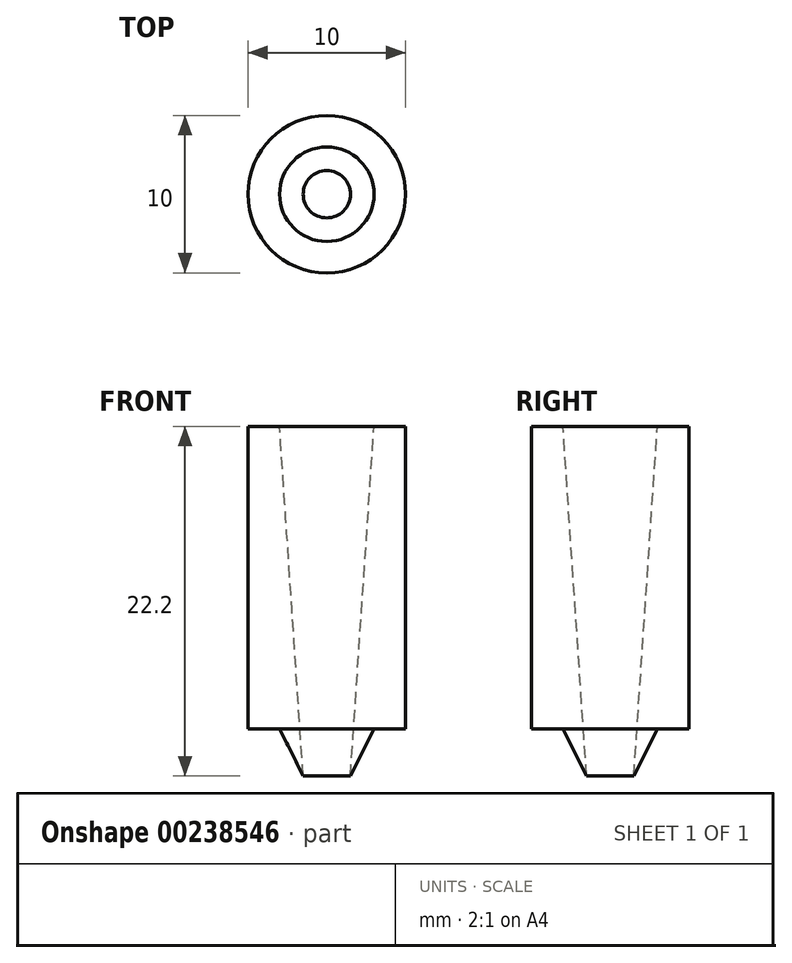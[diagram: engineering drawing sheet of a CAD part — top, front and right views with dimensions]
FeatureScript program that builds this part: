
annotation { "Feature Type Name" : "Feature", "Feature Type Description" : "" }
export const myFeature = defineFeature(function(context is Context, id is Id, definition is map)
    precondition{}
    {
        {
            var Q0;
            Q0=qCreatedBy(makeId("Right.planeOp"),FACE);
            var sketch = newSketch(context, id + "F0", { "sketchPlane" : qUnion([Q0])});
            skLineSegment(sketch, "E0", {"start": v(3, 19.2) * mm, "end": v(5, 19.2) * mm});
            skLineSegment(sketch, "E1", {"start": v(5, 19.2) * mm, "end": v(5, 0) * mm});
            skLineSegment(sketch, "E2", {"start": v(3, 0) * mm, "end": v(1.5, -3) * mm});
            skLineSegment(sketch, "E3", {"start": v(3, 19.2) * mm, "end": v(1.5, -3) * mm});
            skLineSegment(sketch, "E4", {"start": v(3, 0) * mm, "end": v(5, 0) * mm});
            skSolve(sketch);
        }
        {
            var Q0;
            Q0=qCreatedBy(makeId("Right.planeOp"),FACE);
            var sketch = newSketch(context, id + "F1", { "sketchPlane" : qUnion([Q0])});
            skLineSegment(sketch, "E5", {"start": v(0, 0) * mm, "end": v(0, 45.5) * mm});
            skSolve(sketch);
        }
        {
            var Q0;
            Q0=makeQuery(id+"F0.imprint","IMPRINT",FACE,{"disambiguationData":[TD([[makeQuery(id+"F0.imprint","IMPRINT",EDGE,{"derivedFrom":sQuery(id+"F0.wireOp",EDGE,"E0")}),-1.0]])]});
            var Q1;
            Q1=sQuery(id+"F1.wireOp",EDGE,"E5");
            revolve(context, id + "F2", {"entities" : qUnion([Q0]), "axis" : qUnion([Q1]), "revolveType" : RevolveType.FULL});
        }
    });
